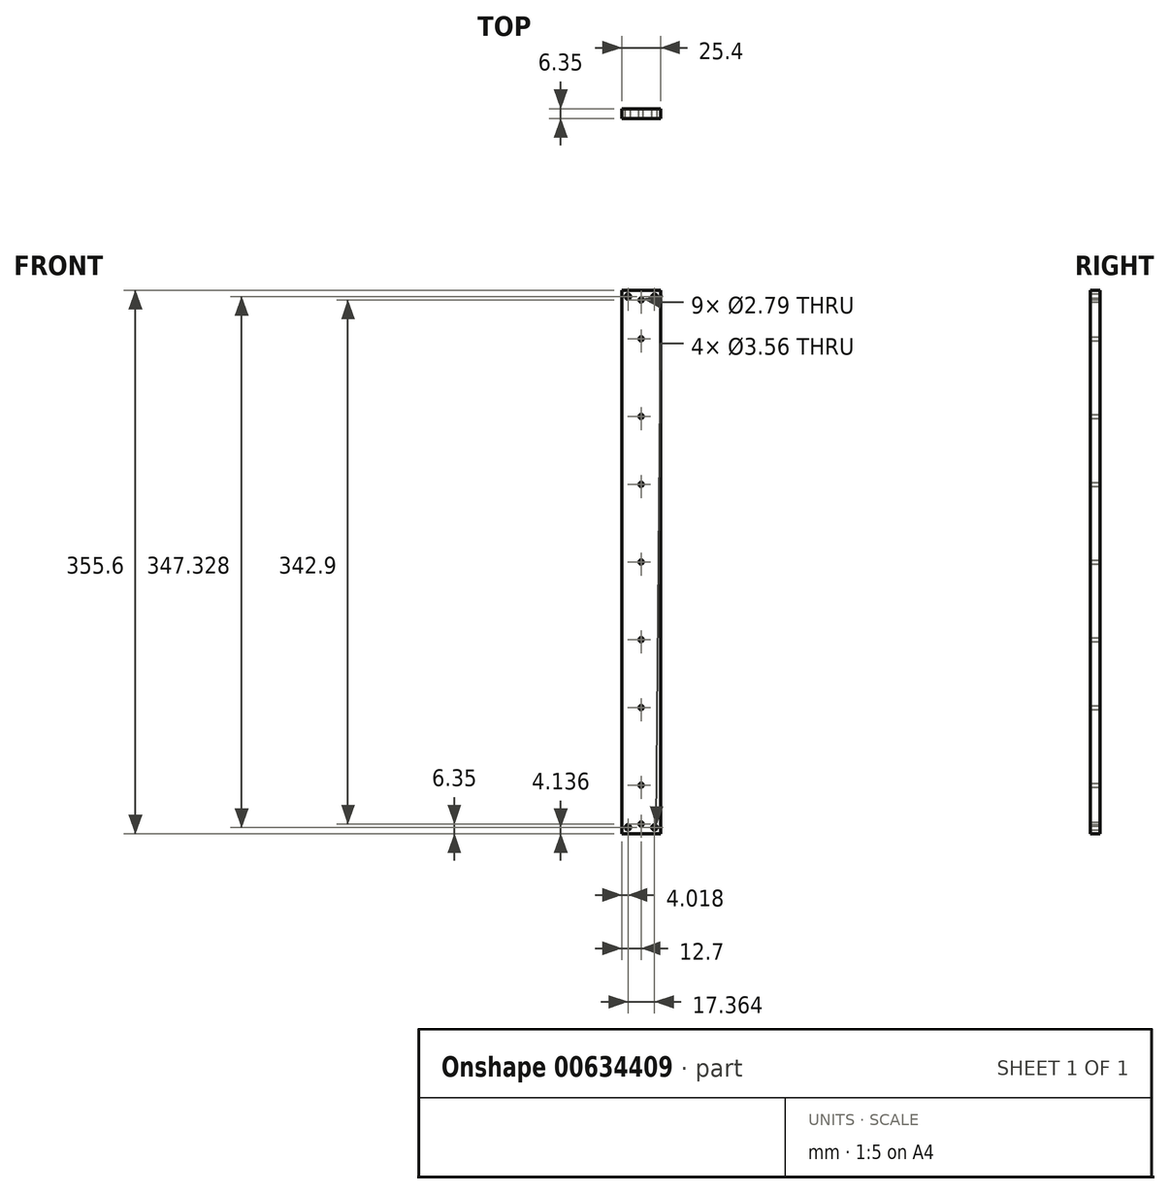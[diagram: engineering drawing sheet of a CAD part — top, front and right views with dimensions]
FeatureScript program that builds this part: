
annotation { "Feature Type Name" : "Feature", "Feature Type Description" : "" }
export const myFeature = defineFeature(function(context is Context, id is Id, definition is map)
    precondition{}
    {
        {
            var Q0;
            Q0=qCreatedBy(makeId("Front.planeOp"),FACE);
            var sketch = newSketch(context, id + "F0", { "sketchPlane" : qUnion([Q0])});
            skLineSegment(sketch, "E0.bottom", {"start": v(12.7, 177.8) * mm, "end": v(-12.7, 177.8) * mm});
            skLineSegment(sketch, "E0.top", {"start": v(12.7, -177.8) * mm, "end": v(-12.7, -177.8) * mm});
            skLineSegment(sketch, "E0.left", {"start": v(12.7, 177.8) * mm, "end": v(12.7, -177.8) * mm});
            skLineSegment(sketch, "E0.right", {"start": v(-12.7, 177.8) * mm, "end": v(-12.7, -177.8) * mm});
            skPoint(sketch, "E0.middle", {"position": v(0, 0) * mm});
            skCircle(sketch, "E1", {"center": v(8.68, 173.66) * mm, "radius": 1.78 * mm});
            skCircle(sketch, "E2.MirrorC", {"center": v(-8.68, 173.66) * mm, "radius": 1.78 * mm});
            skCircle(sketch, "E3.MirrorC", {"center": v(-8.68, -173.66) * mm, "radius": 1.78 * mm});
            skCircle(sketch, "E4.MirrorC", {"center": v(8.68, -173.66) * mm, "radius": 1.78 * mm});
            skCircle(sketch, "E5", {"center": v(0, 171.45) * mm, "radius": 1.4 * mm});
            skPoint(sketch, "E5.centerSnap0", {"position": v(0, 177.8) * mm});
            skLineSegment(sketch, "E6", {"start": v(0, 177.8) * mm, "end": v(0, 171.45) * mm});
            skCircle(sketch, "E7", {"center": v(0, 146.05) * mm, "radius": 1.4 * mm});
            skLineSegment(sketch, "E8", {"start": v(0, 171.45) * mm, "end": v(0, 146.05) * mm});
            skCircle(sketch, "E9", {"center": v(0, 95.25) * mm, "radius": 1.4 * mm});
            skLineSegment(sketch, "E10", {"start": v(0, 146.05) * mm, "end": v(0, 95.25) * mm});
            skCircle(sketch, "E11", {"center": v(0, 0) * mm, "radius": 1.4 * mm});
            skLineSegment(sketch, "E12", {"start": v(0, 50.8) * mm, "end": v(0, 0) * mm});
            skCircle(sketch, "E13", {"center": v(0, 50.8) * mm, "radius": 1.4 * mm});
            skLineSegment(sketch, "E14", {"start": v(-12.7, 0) * mm, "end": v(12.7, 0) * mm});
            skCircle(sketch, "E15.MirrorC", {"center": v(0, -50.8) * mm, "radius": 1.4 * mm});
            skCircle(sketch, "E16.MirrorC", {"center": v(0, -95.25) * mm, "radius": 1.4 * mm});
            skCircle(sketch, "E17.MirrorC", {"center": v(0, -146.05) * mm, "radius": 1.4 * mm});
            skCircle(sketch, "E18.MirrorC", {"center": v(0, -171.45) * mm, "radius": 1.4 * mm});
            skSolve(sketch);
        }
        {
            var Q0;
            Q0 = qSketchRegion(id + "F0", true);
            extrude(context, id + "F1", {"entities" : qUnion([Q0]), "depth" : 6.35 * mm, "offsetDistance" : 25.4 * mm});
        }
    });
